# Revit family: RN 55029 Optipress-Therm-Tappo con valvola di sfiato
name_source: partatom
category: Rohrformteile
units: mm (PartAtom-declared; Revit-internal decimal feet)

## family parameters
Arbeitsebenenbasiert = Nein
Beim Laden mit Abzugskörper schneiden = Nein
Bemaßung runder Anschluss = Durchmesser verwenden
Gemeinsam genutzt = Nein
Immer vertikal = Ja
Teiletyp = Nicht definiert

## types (4) — shared parameters
1.010.00.2 Blattnummer der Richtlinie = 29
1.010.00.3 Ausgabedatum (Monat) der Richtlinie = 201308
1.010.00.4 Herstellername = R. Nussbaum AG
1.010.00.5 Revisionsdatum der Datei = 20190521
1.010.00.6 Webadresse des Herstellers = http://www.nussbaum.ch
1.100.00.4 Produktbezeichnung = Versorgung
1.110.00.2 Index = 1
1.110.00.4 Produktbezeichnung = Optipress-Therm
1.960/3L.00.8 Link (URL) = https://www.nussbaum.ch
29.700.00.4 Produktname = Optipress-Therm-Entlüftungsstopfen
29.700.00.5 Produktkennung = 2
29.700.00.6 Querschnittsform = 1
29.700.00.7 Nennweitensystem = DN
29.700.00.8 Nenndrucksystem = PN
29.710.02.4 Nenndruck = 16
29.710.02.5 max. zul. Überdruck [hPa] = 1600
29.710.02.7 max. zul. Dauer-Betriebsdruck [hPa] = 1600
29.710.02.9 max. zul. Dauer-Betriebstemperatur [°C] = 95
Connector Visibility = Nein
EnclosingSpace Visibility = Nein
Hersteller = R. Nussbaum AG

## per-type parameters (varying)
| type | 1.800.00.3 TGA-Nummer | 1.800.00.4 Kommentarfeld | 1.810.00.3 Hersteller-Bestellnummer | 1.810.00.4 DATANORM-Nummer | 1.810.00.5 StLB-Nummer | 1.810.00.6 GTIN-Nummer | 29.710.02.10 Formstück-Gewicht [kg] | 29.710.02.3 Benennung | CONNECTOR0_DIAMETER_dZ_0r | CONNECTOR0_dZ_01 | CONNECTOR0_ref_dZ | Modell | R. Nussbaum AG 55029.25 de Visibility | R. Nussbaum AG 55029.26 de Visibility | R. Nussbaum AG 55029.27 de Visibility | R. Nussbaum AG 55029.28 de Visibility | Typenkommentare |
| DN=50 | 01900100000000000000000000000000000000000000000019000000000000000004 | 55029.28, Optipress-Therm-Entlüftungsstopfen, DN=50, L=120 | 55029.28 | 55029.28 | 255.678 | 7612945698759 | 0.796 | Optipress-Therm-Entlüftungsstopfen, DN=50, L=120 | 50 mm | 40 mm | 40 mm | 55029.28 | Nein | Nein | Nein | Ja | Optipress-Therm-Tappo con valvola di sfiato DN=50 |
| DN=40 | 01900100000000000000000000000000000000000000000019000000000000000003 | 55029.27, Optipress-Therm-Entlüftungsstopfen, DN=40, L=120 | 55029.27 | 55029.27 | 255.677 | 7612945698742 | 0.6 | Optipress-Therm-Entlüftungsstopfen, DN=40, L=120 | 40 mm | 36 mm | 36 mm | 55029.27 | Nein | Nein | Ja | Nein | Optipress-Therm-Tappo con valvola di sfiato DN=40 |
| DN=32 | 01900100000000000000000000000000000000000000000019000000000000000002 | 55029.26, Optipress-Therm-Entlüftungsstopfen, DN=32, L=100 | 55029.26 | 55029.26 | 255.676 | 7612945698735 | 0.408 | Optipress-Therm-Entlüftungsstopfen, DN=32, L=100 | 32 mm | 26 mm | 26 mm | 55029.26 | Nein | Ja | Nein | Nein | Optipress-Therm-Tappo con valvola di sfiato DN=32 |
| DN=25 | 01900100000000000000000000000000000000000000000019000000000000000001 | 55029.25, Optipress-Therm-Entlüftungsstopfen, DN=25, L=100 | 55029.25 | 55029.25 | 255.675 | 7612945698728 | 0.328 | Optipress-Therm-Entlüftungsstopfen, DN=25, L=100 | 25 mm  [stored 0.082021 ft] | 24 mm | 24 mm | 55029.25 | Ja | Nein | Nein | Nein | Optipress-Therm-Tappo con valvola di sfiato DN=25 |

note: [stored X ft] marks values corroborated as IEEE doubles in the binary element streams (Revit-internal decimal feet)

## geometry (parser evidence)
native form markers: Sweep x1
no freeform markers — native parametric forms only
